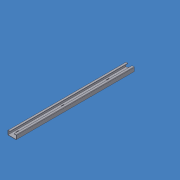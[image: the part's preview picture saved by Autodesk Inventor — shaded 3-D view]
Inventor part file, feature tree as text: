
AUTODESK INVENTOR PART (.ipt)
format: ipt  version: 2015 (Build 190159000, 159)  size: 271,360 bytes
history: native  units: mm
features: sheet_metal_op x9, other x8, sketch x6, plane x2
ambient origin geometry x8: Origin, YZ Plane, XZ Plane, XY Plane, X Axis, Y Axis, Z Axis, Center Point
bodies: Solid1 (feature_tree)
feature tree (25):
  sheet_metal_op  "Face1"
  sheet_metal_op  "Flange1"
  sheet_metal_op  "Flange2"
  sheet_metal_op  "Flange3"
  sheet_metal_op  "Flange4"
  plane  "Work Plane4"
  plane  "Work Plane6"
  sketch  "Sketch1"  dims[d4=0.001mm]
  other  "Plate1"
  sketch  "Sketch2"  dims[d5=3.0mm]
  other  "Plate2"
  sheet_metal_op  "Bend1"
  sketch  "Sketch3"  dims[d6=0.001mm]
  other  "Plate3"
  sheet_metal_op  "Bend2"
  sketch  "Sketch4"  dims[d7=6.0mm]
  other  "Plate4"
  sheet_metal_op  "Bend3"
  sketch  "Sketch5"  dims[d8=0.001mm]
  other  "Plate5"
  sheet_metal_op  "Bend4"
  sketch  "Sketch6"  dims[d9=29.0mm d10=90.0deg d11=0.001mm d12=3.0mm d13=0.001mm d14=6.0mm d15=0.001mm d16=29.0mm d17=90.0deg d18=0.001mm d19=3.0mm d20=0.001mm d21=6.0mm d22=0.001mm d23=15.0mm d24=90.0deg d25=0.001mm d26=3.0mm d27=0.001mm d28=6.0mm d29=0.001mm d30=15.0mm d31=90.0deg d32=0.001mm d33=4.0mm d34=20.5mm d35=4.0mm d36=20.5mm d37=0.0mm d38=33.0mm d40=4.0mm d41=0.0mm d42=950.0mm d45=150.0mm d46=10.0mm d47=10.0mm d48=64.0mm d49=6.0mm d50=64.0mm d51=4.0mm d52=9.0mm d62=20.5mm d63=4.0mm d64=9.0mm d65=20.5mm d66=4.0mm d68=4.0mm d69=0.0mm d71=50.0mm d72=33.0mm d73=16.5mm d74=9.0mm d75=4.0mm d76=20.5mm d77=4.0mm d78=33.0mm d0=3.0mm]
  other  "FlatPattern"
  other  "Cut1"
  other  "FlatPatternExtrusion2"
